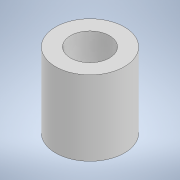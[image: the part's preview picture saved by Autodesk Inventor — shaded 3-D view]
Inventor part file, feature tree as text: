
AUTODESK INVENTOR PART (.ipt)
format: ipt  version: 2022.3 (Build 263350000, 350)  size: 97,792 bytes
history: native  units: mm
features: extrude x1, sketch x1
ambient origin geometry x8: Origin, YZ Plane, XZ Plane, XY Plane, X Axis, Y Axis, Z Axis, Center Point
bodies: Solid1 (feature_tree)
feature tree (2):
  extrude  "Extrusion1"  Depth=10.0mm
  sketch  "Sketch1"  dims[d0=5.2mm d1=2.0mm d2=10.0mm d3=0.0mm]
